# Revit family: Disk Grout
name_source: partatom
category: Structural Columns
units: mm (PartAtom-declared; Revit-internal decimal feet)

## family parameters
Always export as geometry = No
Beam cutback in plan = From geometry
Cut with Voids When Loaded = No
Display in Hidden Views = Edges Hidden by Other Members
Material for Model Behavior = Concrete
OmniClass Number = 23.25.30.11.14.11
OmniClass Title = Columns
Section Shape = Not Defined
Shared = No
Show family pre-cut in plan views = Yes

## types (4) — shared parameters
Anchor material = Concrete, Cast-in-Place gray
D anchor Rod = 63.5 mm
Disk 2 Offset = 1370 mm
Disk Diameter = 350 mm
Disk Material = <By Category>
Grout Material = Concrete, Cast-in-Place gray
Grout Void = 31.75 mm

## per-type parameters (varying)
| type | Anchor Height Offset | D Grout | D Void | Disk 1 Offset | Disk Thickness |
| 300mm | 1995 mm  [stored 6.54528 ft] | 200 mm  [stored 0.656168 ft] | 63.5 mm | 750 mm  [stored 2.46063 ft] | 20 mm  [stored 0.0656168 ft] |
| 450mm | 356.17 mm | 300 mm | 90 mm  [stored 0.295276 ft] | 380 mm | 140 mm |
| 600mm | 356.17 mm | 300 mm | 90 mm  [stored 0.295276 ft] | 380 mm | 140 mm |
| 750mm | 356.17 mm | 300 mm | 90 mm  [stored 0.295276 ft] | 380 mm | 140 mm |

note: [stored X ft] marks values corroborated as IEEE doubles in the binary element streams (Revit-internal decimal feet)

## geometry (parser evidence)
native form markers: Sweep x1
no freeform markers — native parametric forms only
